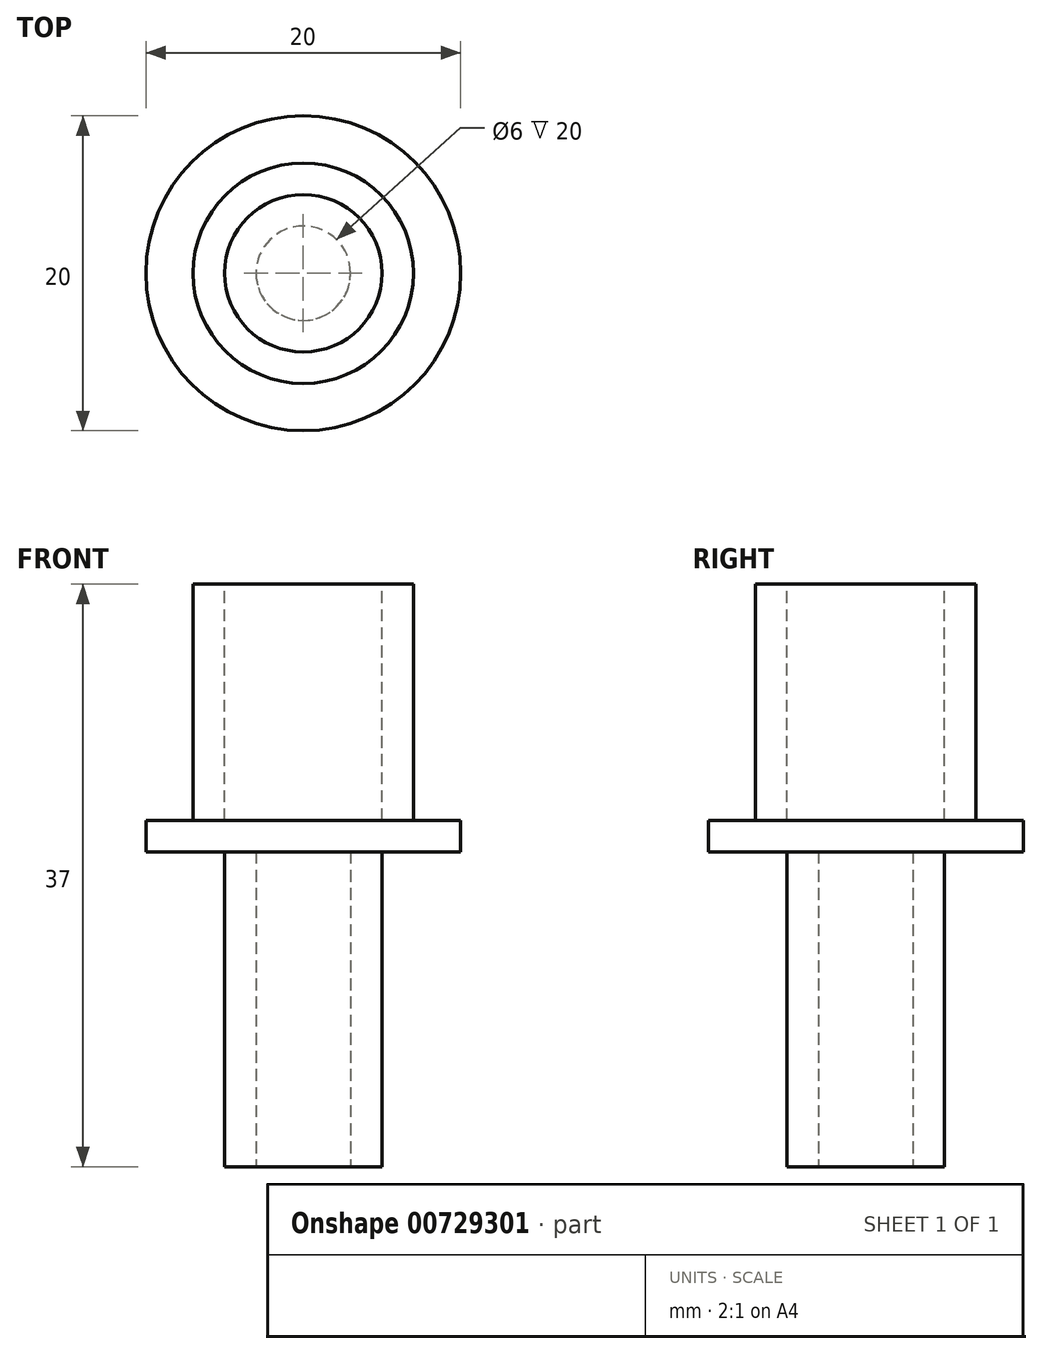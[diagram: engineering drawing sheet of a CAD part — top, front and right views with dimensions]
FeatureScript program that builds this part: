
annotation { "Feature Type Name" : "Feature", "Feature Type Description" : "" }
export const myFeature = defineFeature(function(context is Context, id is Id, definition is map)
    precondition{}
    {
        {
            var Q0;
            Q0=qCreatedBy(makeId("Front.planeOp"),FACE);
            var sketch = newSketch(context, id + "F0", { "sketchPlane" : qUnion([Q0])});
            skLineSegment(sketch, "E0", {"start": v(0, 0) * mm, "end": v(7, 0) * mm});
            skLineSegment(sketch, "E1", {"start": v(7, 0) * mm, "end": v(7, -15) * mm});
            skLineSegment(sketch, "E2", {"start": v(7, -15) * mm, "end": v(10, -15) * mm});
            skLineSegment(sketch, "E3", {"start": v(10, -15) * mm, "end": v(10, -17) * mm});
            skLineSegment(sketch, "E4", {"start": v(10, -17) * mm, "end": v(7, -17) * mm});
            skLineSegment(sketch, "E5", {"start": v(7, -17) * mm, "end": v(5, -17) * mm});
            skLineSegment(sketch, "E6", {"start": v(5, -17) * mm, "end": v(5, -37) * mm});
            skLineSegment(sketch, "E7", {"start": v(5, -37) * mm, "end": v(0, -37) * mm});
            skLineSegment(sketch, "E8", {"start": v(0, -37) * mm, "end": v(0, 0) * mm});
            skSolve(sketch);
        }
        {
            var Q0;
            Q0 = qSketchRegion(id + "F0", true);
            var Q1;
            Q1=sQuery(id+"F0.wireOp",EDGE,"E8");
            revolve(context, id + "F1", {"surfaceOperationType" : NewSurfaceOperationType.NEW, "entities" : qUnion([Q0]), "axis" : qUnion([Q1]), "revolveType" : RevolveType.FULL});
        }
        {
            var Q0;
            Q0=makeQuery(id+"F1.opRevolve","SWEPT_FACE",FACE,{"disambiguationData":[OSD([sQuery(id+"F0.wireOp",EDGE,"E0")])]});
            var sketch = newSketch(context, id + "F2", { "sketchPlane" : qUnion([Q0])});
            skCircle(sketch, "E9", {"center": v(0, 0) * mm, "radius": 5 * mm});
            skSolve(sketch);
        }
        {
            var Q0;
            Q0 = qSketchRegion(id + "F2", true);
            var Q1;
            Q1=makeQuery(id+"F1.opRevolve","SWEPT_FACE",FACE,{"disambiguationData":[OSD([sQuery(id+"F0.wireOp",EDGE,"E2")])]});
            extrude(context, id + "F3", {"entities" : qUnion([Q0]), "operationType" : NewBodyOperationType.REMOVE, "endBound" : BoundingType.UP_TO_SURFACE, "oppositeDirection" : true, "depth" : 25 * mm, "endBoundEntityFace" : qUnion([Q1]), "offsetDistance" : 25 * mm});
        }
        {
            var Q0;
            Q0=makeQuery(id+"F1.opRevolve","SWEPT_FACE",FACE,{"disambiguationData":[OSD([sQuery(id+"F0.wireOp",EDGE,"E7")])]});
            var sketch = newSketch(context, id + "F4", { "sketchPlane" : qUnion([Q0])});
            skCircle(sketch, "E10", {"center": v(0, 0) * mm, "radius": 3 * mm});
            skSolve(sketch);
        }
        {
            var Q0;
            Q0 = qSketchRegion(id + "F4", true);
            var Q1;
            Q1=makeQuery(id+"F1.opRevolve","SWEPT_FACE",FACE,{"disambiguationData":[OSD([sQuery(id+"F0.wireOp",EDGE,"E4"),sQuery(id+"F0.wireOp",EDGE,"E5")])]});
            extrude(context, id + "F5", {"entities" : qUnion([Q0]), "operationType" : NewBodyOperationType.REMOVE, "endBound" : BoundingType.UP_TO_SURFACE, "oppositeDirection" : true, "depth" : 25 * mm, "endBoundEntityFace" : qUnion([Q1]), "offsetDistance" : 25 * mm});
        }
        {
            var Q0;
            Q0=makeQuery(id+"F1.opRevolve","SWEPT_FACE",FACE,{"disambiguationData":[OSD([sQuery(id+"F0.wireOp",EDGE,"E7")])]});
            var sketch = newSketch(context, id + "F6", { "sketchPlane" : qUnion([Q0])});
            skCircle(sketch, "E11", {"center": v(0, 0) * mm, "radius": 2.9 * mm});
            skSolve(sketch);
        }
        {
            var Q0;
            Q0 = qSketchRegion(id + "F6", true);
            extrude(context, id + "F7", {"entities" : qUnion([Q0]), "oppositeDirection" : true, "depth" : 20 * mm, "offsetDistance" : 25 * mm});
        }
        {
            var Q0;
            Q0=makeQuery(id+"F7.opExtrude","SWEPT_BODY",BODY,{"disambiguationData":[OSD([sQuery(id+"F6.wireOp",EDGE,"E11")])]});
            deleteBodies(context, id + "F8", {"entities" : qUnion([Q0])});
        }
    });
